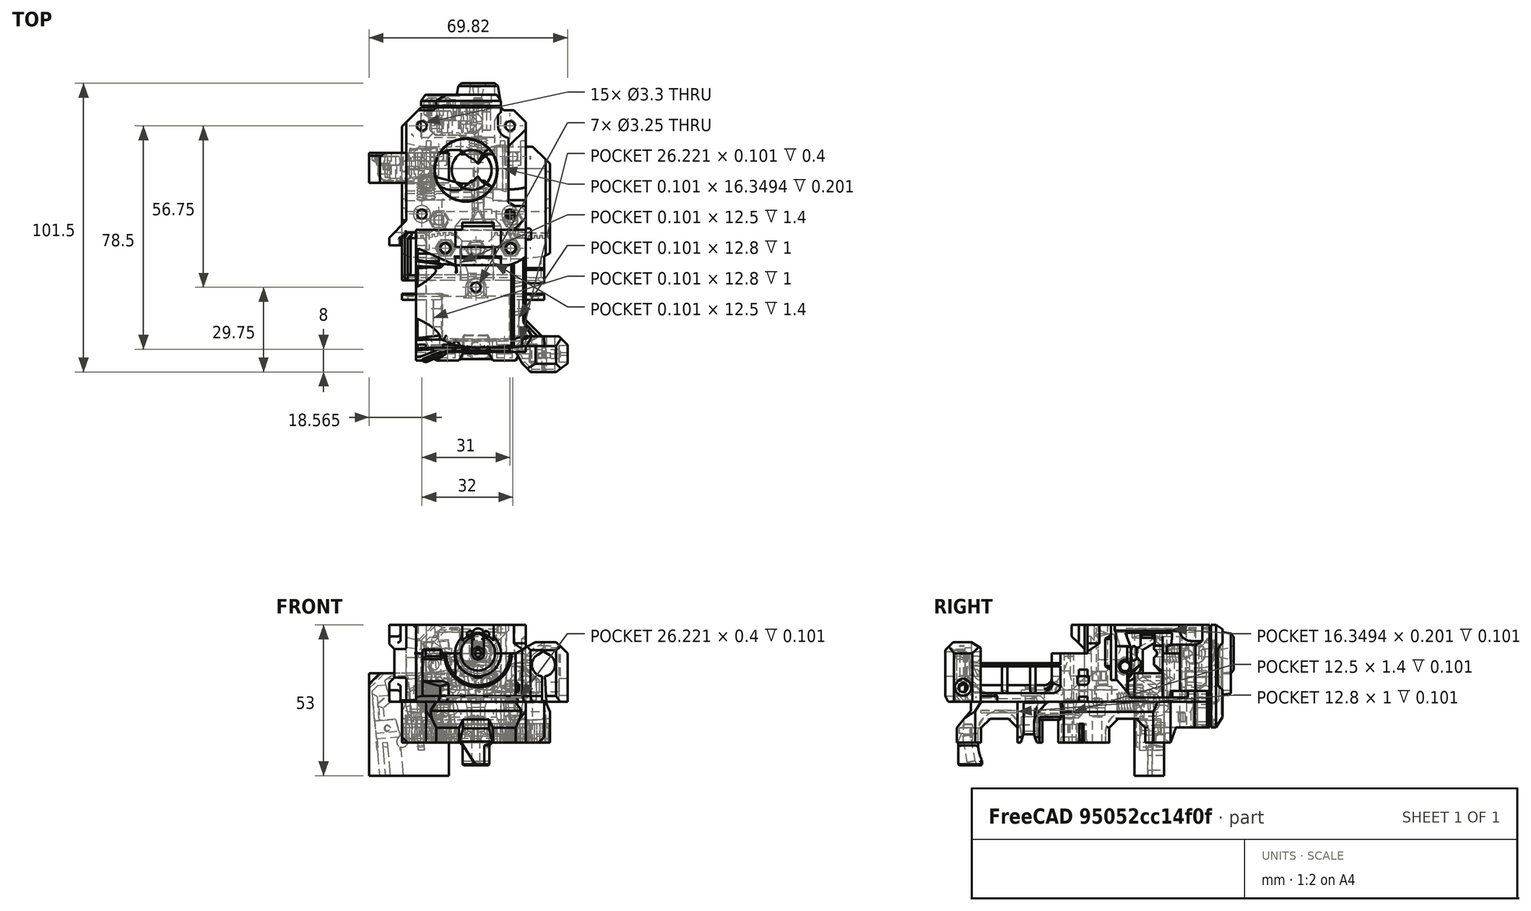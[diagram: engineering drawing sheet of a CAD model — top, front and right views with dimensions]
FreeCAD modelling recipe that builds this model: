
FCSTD DOCUMENT  (FreeCAD 0.18R14555 (Git shallow))
Label: filament-sensor-remote-mount
License: All rights reserved
LicenseURL: http://en.wikipedia.org/wiki/All_rights_reserved
objects: Part::Feature×13, Part::Box×6, Part::Cut×4, Part::MultiFuse×4, Part::Cylinder×3, Part::MultiCommon×1, Part::Chamfer×1
note: 32 computed .brp shape members not serialized (recipe doc carries the construction recipe); baked Part::Feature solids carry a one-line shape summary decoded from their .brp

FEATURE [Part::Feature] Part__Feature023  label="body"
  Placement = pos=(14.025,4.5,-6.08082e-11) rot=(0,0,1;0rad)
  shape: bbox 64.24 x 94.52 x 27.72 mm, 732 faces (baked)
FEATURE [Part::Box] Box  label="Cube"
  AttacherType = Attacher::AttachEngine3D
  Height = 29
  Length = 28.1
  Placement = pos=(-1.77,16,0) rot=(0,0,1;0rad)
  Width = 13
FEATURE [Part::Box] Box001  label="Cube001"
  AttacherType = Attacher::AttachEngine3D
  Height = 27
  Length = 5
  Placement = pos=(-6.77,17.5,0) rot=(0,0,1;0rad)
  Width = 7
FEATURE [Part::Feature] Part__Feature024  label="body001"
  Placement = pos=(14.025,4.5,-6.08082e-11) rot=(0,0,1;0rad)
  shape: bbox 64.24 x 94.52 x 27.72 mm, 732 faces (baked)
FEATURE [Part::Cylinder] Cylinder
  Angle = 360
  AttacherType = Attacher::AttachEngine3D
  Height = 27
  Placement = pos=(-1,20,0) rot=(0,0,1;0rad)
  Radius = 2.2
FEATURE [Part::Feature] Part__Feature  label="1"
  shape: bbox 11.55 x 19.8 x 11.8 mm, 29 faces (baked)
FEATURE [Part::Cylinder] Cylinder001
  Angle = 360
  AttacherType = Attacher::AttachEngine3D
  Height = 6
  Radius = 4.5
FEATURE [Part::Cut] Cut001  label="m6-thread"
  Base = -> Cylinder001
  Tool = -> Part__Feature
FEATURE [Part::Feature] Cut001001  label="m6-thread001"
  Placement = pos=(18.27,16,17) rot=(1,0,0;1.5708rad)
  shape: bbox 6.606 x 6.902 x 6.606 mm, 9 faces (baked)
FEATURE [Part::Feature] Cut001002  label="m6-thread002"
  Placement = pos=(0,0,0) rot=(1,0,0;1.5708rad)
  shape: bbox 6.606 x 6.902 x 6.606 mm, 9 faces (baked)
FEATURE [Part::Cylinder] Cylinder002
  Angle = 360
  AttacherType = Attacher::AttachEngine3D
  Height = 6
  Placement = pos=(18.27,10,17) rot=(-1,0,0;1.5708rad)
  Radius = 6
FEATURE [Part::Box] Box002  label="Cube002"
  AttacherType = Attacher::AttachEngine3D
  Height = 17
  Length = 12
  Placement = pos=(12.27,10,0) rot=(0,0,1;0rad)
  Width = 6
FEATURE [Part::Feature] Part__Feature050  label="fs_cover v28"
  Placement = pos=(-1.775,31,27) rot=(-1,0,0;1.5708rad)
  shape: bbox 28.1 x 8 x 36 mm, 236 faces (baked)
FEATURE [Part::Box] Box003  label="Cube003"
  AttacherType = Attacher::AttachEngine3D
  Height = 9
  Length = 28.1
  Placement = pos=(-1.77,16,-9) rot=(0,0,1;0rad)
  Width = 10.5
FEATURE [Part::MultiCommon] Common
  Shapes = -> [Part__Feature023,Box]
FEATURE [Part::Cut] Cut
  Base = -> Cylinder
  Tool = -> Box001
FEATURE [Part::MultiFuse] Fusion
  Shapes = -> [Common,Cut]
FEATURE [Part::Box] Box004  label="Cube004"
  AttacherType = Attacher::AttachEngine3D
  Height = 27
  Length = 3.33
  Placement = pos=(23,16,0) rot=(0,0,1;0rad)
  Width = 10.5
FEATURE [Part::MultiFuse] Fusion001
  Shapes = -> [Fusion,Box004]
FEATURE [Part::Feature] Part__Feature017  label="x_carriage"
  Placement = pos=(43.525,26.5,-9.9e-15) rot=(0.707107,-0.707107,0;3.14159rad)
  shape: bbox 52.02 x 89.02 x 23.37 mm, 724 faces (baked)
FEATURE [Part::Box] Box005  label="Cube005"
  AttacherType = Attacher::AttachEngine3D
  Height = 7
  Length = 11.1
  Placement = pos=(0.23,20,-8) rot=(0,0,1;0rad)
  Width = 6.5
FEATURE [Part::Cut] Cut001003
  Base = -> Box005
  Tool = -> Part__Feature017
FEATURE [Part::Feature] Cut001003001  label="Cut001004"
  Placement = pos=(-0.08716,0,1) rot=(0,0,1;0rad)
  shape: bbox 9.045 x 5.8 x 7 mm, 10 faces (baked)
FEATURE [Part::Feature] Part__Feature051  label="x_carriage001"
  Placement = pos=(43.525,26.5,-1e-14) rot=(0.707107,-0.707107,0;3.14159rad)
  shape: bbox 52.02 x 89.02 x 23.37 mm, 724 faces (baked)
FEATURE [Part::Feature] Cut001003002  label="Cut001005"
  Placement = pos=(0.08716,0,-1) rot=(0,0,1;0rad)
  shape: bbox 9.045 x 5.8 x 7 mm, 10 faces (baked)
FEATURE [Part::MultiFuse] Fusion002
  Shapes = -> [Cut001003001,Cut001003002]
FEATURE [Part::Cut] Cut001003003
  Base = -> Box003
  Tool = -> Fusion002
FEATURE [Part::Feature] Cut001003003001  label="Cut001003004"
  shape: bbox 28.1 x 10.5 x 9 mm, 22 faces (baked)
FEATURE [Part::MultiFuse] Fusion003
  Placement = pos=(-18.27,-16,-17) rot=(0,0,1;0rad)
  Shapes = -> [Cut001003003001,Fusion001]
FEATURE [Part::Feature] Fusion003001  label="Fusion004"
  shape: bbox 28.11 x 12.01 x 36.01 mm, 119 faces (baked)
FEATURE [Part::Chamfer] Chamfer
  Base = -> Fusion003001
  Edges = 1 edges r=3.85: [Edge8]
FEATURE [Part::Feature] Chamfer001
  shape: bbox 28.11 x 12.01 x 36.01 mm, 120 faces (baked)
